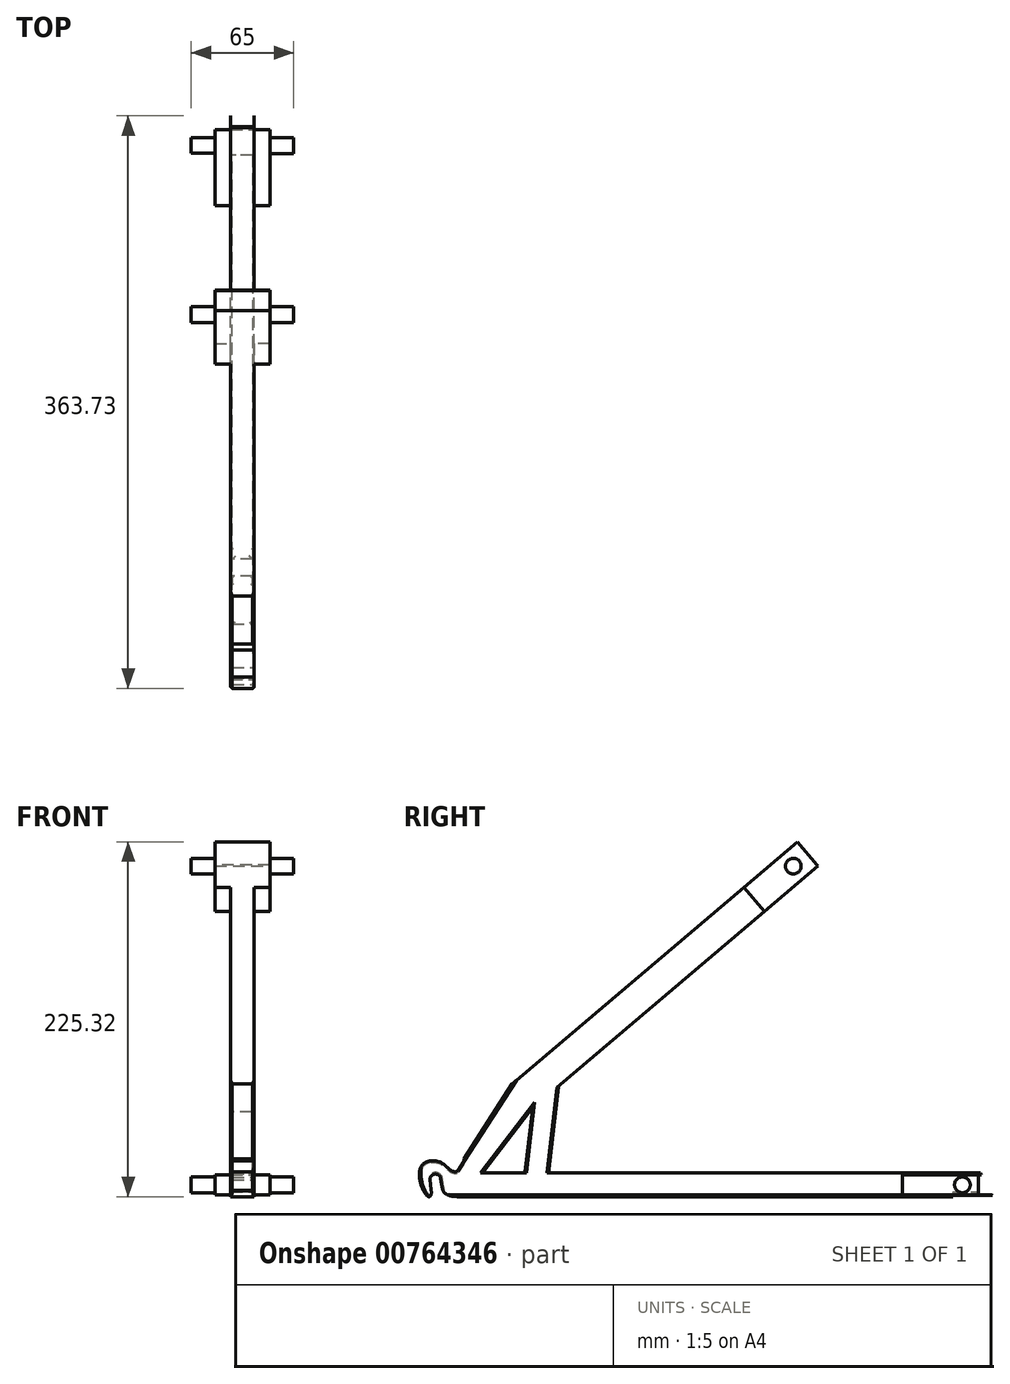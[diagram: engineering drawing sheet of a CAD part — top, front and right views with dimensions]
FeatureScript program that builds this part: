
annotation { "Feature Type Name" : "Feature", "Feature Type Description" : "" }
export const myFeature = defineFeature(function(context is Context, id is Id, definition is map)
    precondition{}
    {
        {
            var Q0;
            Q0=qCreatedBy(makeId("Right.planeOp"),FACE);
            var sketch = newSketch(context, id + "F0", { "sketchPlane" : qUnion([Q0])});
            skLineSegment(sketch, "E0", {"start": v(47.78, 0) * mm, "end": v(315.63, 0) * mm});
            skLineSegment(sketch, "E1", {"start": v(48.64, 41.27) * mm, "end": v(16.93, 0) * mm});
            skLineSegment(sketch, "E2", {"start": v(16.93, 0) * mm, "end": v(47.78, 0) * mm});
            skLineSegment(sketch, "E3.bottom", {"start": v(315.63, 0) * mm, "end": v(16.93, 0) * mm});
            skLineSegment(sketch, "E3.top", {"start": v(315.63, -15) * mm, "end": v(16.93, -15) * mm});
            skLineSegment(sketch, "E3.right", {"start": v(16.93, 0) * mm, "end": v(16.93, -15) * mm});
            skLineSegment(sketch, "E4.left", {"start": v(48.64, 41.27) * mm, "end": v(43.82, 0) * mm});
            skLineSegment(sketch, "E5", {"start": v(48.64, 41.27) * mm, "end": v(35.7, 56.52) * mm});
            skLineSegment(sketch, "E6", {"start": v(16.93, 0) * mm, "end": v(5.04, 9.14) * mm});
            skLineSegment(sketch, "E7", {"start": v(5.04, 9.14) * mm, "end": v(35.7, 56.52) * mm});
            skLineSegment(sketch, "E8", {"start": v(43.82, 0) * mm, "end": v(58.82, 0) * mm});
            skLineSegment(sketch, "E9", {"start": v(58.82, 0) * mm, "end": v(65.3, 55.4) * mm});
            skLineSegment(sketch, "E10", {"start": v(65.3, 55.4) * mm, "end": v(48.64, 41.27) * mm});
            skLineSegment(sketch, "E11", {"start": v(16.93, -15) * mm, "end": v(5.04, -15) * mm});
            skLineSegment(sketch, "E12", {"start": v(5.04, -15) * mm, "end": v(5.04, 9.14) * mm});
            skLineSegment(sketch, "E13", {"start": v(315.63, -15) * mm, "end": v(315.63, 0) * mm});
            skPoint(sketch, "E14", {"position": v(131.02, 137.39) * mm});
            skPoint(sketch, "E15", {"position": v(143.96, 122.14) * mm});
            skPoint(sketch, "E16", {"position": v(115.77, 124.45) * mm});
            skPoint(sketch, "E17", {"position": v(128.7, 109.2) * mm});
            skPoint(sketch, "E18", {"position": v(159.2, 135.07) * mm});
            skPoint(sketch, "E19", {"position": v(146.27, 150.33) * mm});
            skLineSegment(sketch, "E20", {"start": v(128.7, 109.2) * mm, "end": v(115.77, 124.45) * mm});
            skLineSegment(sketch, "E21", {"start": v(35.7, 56.52) * mm, "end": v(48.64, 41.27) * mm});
            skLineSegment(sketch, "E22", {"start": v(146.27, 150.33) * mm, "end": v(159.2, 135.07) * mm});
            skLineSegment(sketch, "E23", {"start": v(35.7, 56.52) * mm, "end": v(115.77, 124.45) * mm});
            skLineSegment(sketch, "E24", {"start": v(65.3, 55.4) * mm, "end": v(128.7, 109.2) * mm});
            skLineSegment(sketch, "E25", {"start": v(115.77, 124.45) * mm, "end": v(146.27, 150.33) * mm});
            skLineSegment(sketch, "E26", {"start": v(128.7, 109.2) * mm, "end": v(159.2, 135.07) * mm});
            skLineSegment(sketch, "E27", {"start": v(229.92, 195.06) * mm, "end": v(216.98, 210.32) * mm});
            skLineSegment(sketch, "E28", {"start": v(159.2, 135.07) * mm, "end": v(229.92, 195.06) * mm});
            skLineSegment(sketch, "E29", {"start": v(216.98, 210.32) * mm, "end": v(146.27, 150.33) * mm});
            skLineSegment(sketch, "E30", {"start": v(340.63, 0) * mm, "end": v(340.63, -15) * mm});
            skLineSegment(sketch, "E31", {"start": v(315.63, 0) * mm, "end": v(340.63, 0) * mm});
            skLineSegment(sketch, "E32", {"start": v(340.63, -15) * mm, "end": v(315.63, -15) * mm});
            skSolve(sketch);
        }
        {
            var Q0;
            {var subQ1=sQuery(id+"F0.wireOp",EDGE,"Yo74uOjQ-i0EO-3RHr-a7oa-XagKDitOUhVE");Q0=makeQuery(id+"F0.imprint","IMPRINT",FACE,{"disambiguationData":[TD([[makeQuery(id+"F0.imprint","IMPRINT",EDGE,{"derivedFrom":subQ1}),1.0]])]});}
            var Q1;
            {var subQ1=sQuery(id+"F0.wireOp",EDGE,"E6");Q1=makeQuery(id+"F0.imprint","IMPRINT",FACE,{"disambiguationData":[TD([[makeQuery(id+"F0.imprint","IMPRINT",EDGE,{"derivedFrom":subQ1}),-1.0]])]});}
            var Q2;
            Q2=makeQuery(id+"F0.imprint","IMPRINT",FACE,{"disambiguationData":[TD([[makeQuery(id+"F0.imprint","IMPRINT",EDGE,{"derivedFrom":sQuery(id+"F0.wireOp",EDGE,"E3.right")}),-1.0]])]});
            var Q3;
            Q3=makeQuery(id+"F0.imprint","IMPRINT",FACE,{"disambiguationData":[TD([[makeQuery(id+"F0.imprint","IMPRINT",EDGE,{"derivedFrom":sQuery(id+"F0.wireOp",EDGE,"E3.top")}),-1.0]])]});
            var Q4;
            {var subQ0=sQuery(id+"F0.wireOp",EDGE,"E4.left");Q4=makeQuery(id+"F0.imprint","IMPRINT",FACE,{"disambiguationData":[TD([[makeQuery(id+"F0.imprint","IMPRINT",EDGE,{"derivedFrom":subQ0}),1.0]])]});}
            var Q5;
            {var subQ3=sQuery(id+"F0.wireOp",EDGE,"RTDkQwoI-wCG5-Ql9m-PHR5-vW7OaOIPGGAD.top");Q5=makeQuery(id+"F0.imprint","IMPRINT",FACE,{"disambiguationData":[TD([[makeQuery(id+"F0.imprint","IMPRINT",EDGE,{"derivedFrom":subQ3}),-1.0]])]});}
            var Q6;
            {var subQ1=sQuery(id+"F0.wireOp",EDGE,"E1");var subQ3=sQuery(id+"F0.wireOp",EDGE,"RTDkQwoI-wCG5-Ql9m-PHR5-vW7OaOIPGGAD.left");var subQ4=makeQuery(id+"F0.imprint","INTERSECT",VERTEX,{"derivedFrom":[subQ1,subQ3]});Q6=makeQuery(id+"F0.imprint","IMPRINT",FACE,{"disambiguationData":[TD([[makeQuery(id+"F0.imprint","IMPRINT",EDGE,{"disambiguationData":[TD([[subQ4,-1.0]])],"derivedFrom":subQ3}),-1.0]])]});}
            var Q7;
            {var subQ0=sQuery(id+"F0.wireOp",EDGE,"o3pL6dEJ-hwyi-6mrB-k6X7-aminsl83ahjA");Q7=makeQuery(id+"F0.imprint","IMPRINT",FACE,{"disambiguationData":[TD([[makeQuery(id+"F0.imprint","IMPRINT",EDGE,{"derivedFrom":subQ0}),-1.0]])]});}
            var Q8;
            {var subQ0=sQuery(id+"F0.wireOp",EDGE,"o3pL6dEJ-hwyi-6mrB-k6X7-aminsl83ahjA");Q8=makeQuery(id+"F0.imprint","IMPRINT",FACE,{"disambiguationData":[TD([[makeQuery(id+"F0.imprint","IMPRINT",EDGE,{"derivedFrom":subQ0}),1.0]])]});}
            var Q9;
            Q9=makeQuery(id+"F0.imprint","IMPRINT",FACE,{"disambiguationData":[TD([[makeQuery(id+"F0.imprint","IMPRINT",EDGE,{"derivedFrom":sQuery(id+"F0.wireOp",EDGE,"Yo74uOjQ-i0EO-3RHr-a7oa-XagKDitOUhVE")}),-1.0]])]});
            var Q10;
            Q10=makeQuery(id+"F0.imprint","IMPRINT",FACE,{"disambiguationData":[TD([[makeQuery(id+"F0.imprint","IMPRINT",EDGE,{"derivedFrom":sQuery(id+"F0.wireOp",EDGE,"WOJb4iod-LhNt-r6cw-RdzF-wMDI1TDEllQv.bottom")}),-1.0]])]});
            var Q11;
            Q11=makeQuery(id+"F0.imprint","IMPRINT",FACE,{"disambiguationData":[TD([[makeQuery(id+"F0.imprint","IMPRINT",EDGE,{"derivedFrom":sQuery(id+"F0.wireOp",EDGE,"WOJb4iod-LhNt-r6cw-RdzF-wMDI1TDEllQv.right")}),1.0]])]});
            var Q12;
            {var subQ0=sQuery(id+"F0.wireOp",EDGE,"E3.right");Q12=makeQuery(id+"F0.imprint","IMPRINT",FACE,{"disambiguationData":[TD([[makeQuery(id+"F0.imprint","IMPRINT",EDGE,{"derivedFrom":subQ0}),1.0]])]});}
            var Q13;
            {var subQ3=sQuery(id+"F0.wireOp",EDGE,"hnlP5vd8-Fwl7-W3YU-HfNq-rofw2tE7fOju");Q13=makeQuery(id+"F0.imprint","IMPRINT",FACE,{"disambiguationData":[TD([[makeQuery(id+"F0.imprint","IMPRINT",EDGE,{"derivedFrom":subQ3}),-1.0]])]});}
            var Q14;
            {var subQ4=sQuery(id+"F0.wireOp",EDGE,"zAPuBMNa-KC0v-FcAM-JJp2-Pc91iyWnGTPB");Q14=makeQuery(id+"F0.imprint","IMPRINT",FACE,{"disambiguationData":[TD([[makeQuery(id+"F0.imprint","IMPRINT",EDGE,{"derivedFrom":subQ4}),-1.0]])]});}
            var Q15;
            {var subQ0=sQuery(id+"F0.wireOp",EDGE,"E3.left");Q15=makeQuery(id+"F0.imprint","IMPRINT",FACE,{"disambiguationData":[TD([[makeQuery(id+"F0.imprint","IMPRINT",EDGE,{"derivedFrom":subQ0}),1.0]])]});}
            var Q16;
            Q16=makeQuery(id+"F0.imprint","IMPRINT",FACE,{"disambiguationData":[TD([[makeQuery(id+"F0.imprint","IMPRINT",EDGE,{"derivedFrom":sQuery(id+"F0.wireOp",EDGE,"E13")}),-1.0]])]});
            var Q17;
            {var subQ2=sQuery(id+"F0.wireOp",EDGE,"Ca3xsWQE-v9L8-s7Dv-516f-RN1bA1puj8tS");Q17=makeQuery(id+"F0.imprint","IMPRINT",FACE,{"disambiguationData":[TD([[makeQuery(id+"F0.imprint","IMPRINT",EDGE,{"derivedFrom":subQ2}),1.0]])]});}
            var Q18;
            {var subQ0=sQuery(id+"F0.wireOp",EDGE,"dxAtwFGu-dCJm-7jaL-4A4g-HOkAJ22Vz9y7");var subQ1=sQuery(id+"F0.wireOp",EDGE,"8YUn9cvo-RZEs-pOM1-VRL8-89LIzTiUGwx0");var subQ2=makeQuery(id+"F0.imprint","INTERSECT",VERTEX,{"derivedFrom":[subQ1,subQ0]});Q18=makeQuery(id+"F0.imprint","IMPRINT",FACE,{"disambiguationData":[TD([[makeQuery(id+"F0.imprint","IMPRINT",EDGE,{"disambiguationData":[TD([[subQ2,-1.0]])],"derivedFrom":subQ0}),1.0]])]});}
            var Q19;
            {var subQ5=sQuery(id+"F0.wireOp",EDGE,"L5jN4jJu-Q4wT-aSny-XyIM-LaIA1ToUzlHX");Q19=makeQuery(id+"F0.imprint","IMPRINT",FACE,{"disambiguationData":[TD([[makeQuery(id+"F0.imprint","IMPRINT",EDGE,{"derivedFrom":subQ5}),1.0]])]});}
            var Q20;
            Q20=makeQuery(id+"F0.imprint","IMPRINT",FACE,{"disambiguationData":[TD([[makeQuery(id+"F0.imprint","IMPRINT",EDGE,{"derivedFrom":sQuery(id+"F0.wireOp",EDGE,"E10")}),-1.0]])]});
            var Q21;
            Q21=makeQuery(id+"F0.imprint","IMPRINT",FACE,{"disambiguationData":[TD([[makeQuery(id+"F0.imprint","IMPRINT",EDGE,{"derivedFrom":sQuery(id+"F0.wireOp",EDGE,"E22")}),1.0]])]});
            var Q22;
            Q22=makeQuery(id+"F0.imprint","IMPRINT",FACE,{"disambiguationData":[TD([[makeQuery(id+"F0.imprint","IMPRINT",EDGE,{"derivedFrom":sQuery(id+"F0.wireOp",EDGE,"E20")}),-1.0]])]});
            extrude(context, id + "F1", {"entities" : qUnion([Q0, Q1, Q2, Q3, Q4, Q5, Q6, Q7, Q8, Q9, Q10, Q11, Q12, Q13, Q14, Q15, Q16, Q17, Q18, Q19, Q20, Q21, Q22]), "depth" : 15 * mm, "offsetDistance" : 25 * mm});
        }
        {
            var Q0;
            {var subQ0=sQuery(id+"F0.wireOp",EDGE,"E3.bottom");Q0=makeQuery(id+"F1.opExtrude","CAP_EDGE",EDGE,{"disambiguationData":[OSD([subQ0]),TDD([makeQuery(id+"F0.imprint","IMPRINT",EDGE,{"disambiguationData":[TD([[makeQuery(id+"F0.imprint","INTERSECT",VERTEX,{"derivedFrom":[subQ0,sQuery(id+"F0.wireOp",EDGE,"E3.left")]}),-1.0]])],"derivedFrom":subQ0})])],"isStart":false});}
            var Q1;
            {var subQ0=sQuery(id+"F0.wireOp",EDGE,"E3.bottom");Q1=makeQuery(id+"F1.opExtrude","CAP_EDGE",EDGE,{"disambiguationData":[OSD([subQ0]),TDD([makeQuery(id+"F0.imprint","IMPRINT",EDGE,{"disambiguationData":[TD([[makeQuery(id+"F0.imprint","INTERSECT",VERTEX,{"derivedFrom":[subQ0,sQuery(id+"F0.wireOp",EDGE,"E3.left")]}),-1.0]])],"derivedFrom":subQ0})])],"isStart":true});}
            var Q2;
            Q2=makeQuery(id+"F1.opExtrude","CAP_EDGE",EDGE,{"disambiguationData":[OSD([sQuery(id+"F0.wireOp",EDGE,"E3.top")])],"isStart":true});
            var Q3;
            Q3=makeQuery(id+"F1.opExtrude","CAP_EDGE",EDGE,{"disambiguationData":[OSD([sQuery(id+"F0.wireOp",EDGE,"E3.top")])],"isStart":false});
            var Q4;
            Q4=makeQuery(id+"F1.opExtrude","CAP_EDGE",EDGE,{"disambiguationData":[OSD([sQuery(id+"F0.wireOp",EDGE,"E3.left")])],"isStart":false});
            var Q5;
            Q5=makeQuery(id+"F1.opExtrude","SWEPT_EDGE",EDGE,{"disambiguationData":[OSD([sQuery(id+"F0.wireOp",EDGE,"E3.bottom"),sQuery(id+"F0.wireOp",EDGE,"E3.left")])]});
            var Q6;
            Q6=makeQuery(id+"F1.opExtrude","CAP_EDGE",EDGE,{"disambiguationData":[OSD([sQuery(id+"F0.wireOp",EDGE,"E3.left")])],"isStart":true});
            var Q7;
            Q7=makeQuery(id+"F1.opExtrude","SWEPT_EDGE",EDGE,{"disambiguationData":[OSD([sQuery(id+"F0.wireOp",EDGE,"E3.top"),sQuery(id+"F0.wireOp",EDGE,"E3.left")])]});
            var Q8;
            Q8=makeQuery(id+"F1.opExtrude","CAP_EDGE",EDGE,{"disambiguationData":[OSD([sQuery(id+"F0.wireOp",EDGE,"d41c5ef0-c10e-4e75-b374-802d414c0d57")])],"isStart":false});
            var Q9;
            Q9=makeQuery(id+"F1.opExtrude","CAP_EDGE",EDGE,{"disambiguationData":[OSD([sQuery(id+"F0.wireOp",EDGE,"d41c5ef0-c10e-4e75-b374-802d414c0d57")])],"isStart":true});
            var Q10;
            Q10=makeQuery(id+"F1.opExtrude","CAP_EDGE",EDGE,{"disambiguationData":[OSD([sQuery(id+"F0.wireOp",EDGE,"E1")])],"isStart":false});
            var Q11;
            Q11=makeQuery(id+"F1.opExtrude","CAP_EDGE",EDGE,{"disambiguationData":[OSD([sQuery(id+"F0.wireOp",EDGE,"E4.left")])],"isStart":false});
            var Q12;
            {var subQ0=sQuery(id+"F0.wireOp",EDGE,"E3.bottom");Q12=makeQuery(id+"F1.opExtrude","CAP_EDGE",EDGE,{"disambiguationData":[OSD([subQ0]),TDD([makeQuery(id+"F0.imprint","IMPRINT",EDGE,{"disambiguationData":[TD([[makeQuery(id+"F0.imprint","INTERSECT",VERTEX,{"derivedFrom":[subQ0,sQuery(id+"F0.wireOp",EDGE,"E4.left"),sQuery(id+"F0.wireOp",EDGE,"E8")]}),-1.0]])],"derivedFrom":subQ0})])],"isStart":false});}
            var Q13;
            Q13=makeQuery(id+"F1.opExtrude","CAP_EDGE",EDGE,{"disambiguationData":[OSD([sQuery(id+"F0.wireOp",EDGE,"E9")])],"isStart":false});
            var Q14;
            Q14=makeQuery(id+"F1.opExtrude","CAP_EDGE",EDGE,{"disambiguationData":[OSD([sQuery(id+"F0.wireOp",EDGE,"E7")])],"isStart":false});
            var Q15;
            Q15=makeQuery(id+"F1.opExtrude","CAP_EDGE",EDGE,{"disambiguationData":[OSD([sQuery(id+"F0.wireOp",EDGE,"E7")])],"isStart":true});
            var Q16;
            Q16=makeQuery(id+"F1.opExtrude","CAP_EDGE",EDGE,{"disambiguationData":[OSD([sQuery(id+"F0.wireOp",EDGE,"E1")])],"isStart":true});
            var Q17;
            Q17=makeQuery(id+"F1.opExtrude","CAP_EDGE",EDGE,{"disambiguationData":[OSD([sQuery(id+"F0.wireOp",EDGE,"E4.left")])],"isStart":true});
            var Q18;
            {var subQ0=sQuery(id+"F0.wireOp",EDGE,"E3.bottom");Q18=makeQuery(id+"F1.opExtrude","CAP_EDGE",EDGE,{"disambiguationData":[OSD([subQ0]),TDD([makeQuery(id+"F0.imprint","IMPRINT",EDGE,{"disambiguationData":[TD([[makeQuery(id+"F0.imprint","INTERSECT",VERTEX,{"derivedFrom":[subQ0,sQuery(id+"F0.wireOp",EDGE,"E4.left"),sQuery(id+"F0.wireOp",EDGE,"E8")]}),-1.0]])],"derivedFrom":subQ0})])],"isStart":true});}
            var Q19;
            Q19=makeQuery(id+"F1.opExtrude","CAP_EDGE",EDGE,{"disambiguationData":[OSD([sQuery(id+"F0.wireOp",EDGE,"E9")])],"isStart":true});
            var Q20;
            Q20=makeQuery(id+"F1.opExtrude","CAP_EDGE",EDGE,{"disambiguationData":[OSD([sQuery(id+"F0.wireOp",EDGE,"uIqcDY9T-Jbxf-aRt4-gg0R-6jHuYA81VSVm")])],"isStart":true});
            var Q21;
            Q21=makeQuery(id+"F1.opExtrude","CAP_EDGE",EDGE,{"disambiguationData":[OSD([sQuery(id+"F0.wireOp",EDGE,"uIqcDY9T-Jbxf-aRt4-gg0R-6jHuYA81VSVm")])],"isStart":false});
            var Q22;
            Q22=makeQuery(id+"F1.opExtrude","CAP_EDGE",EDGE,{"disambiguationData":[OSD([sQuery(id+"F0.wireOp",EDGE,"rEmcZTTS-8Wlh-duEK-OSmW-KXRGUTnN0HfS")])],"isStart":true});
            var Q23;
            Q23=makeQuery(id+"F1.opExtrude","CAP_EDGE",EDGE,{"disambiguationData":[OSD([sQuery(id+"F0.wireOp",EDGE,"rEmcZTTS-8Wlh-duEK-OSmW-KXRGUTnN0HfS")])],"isStart":false});
            var Q24;
            Q24=makeQuery(id+"F1.opExtrude","CAP_EDGE",EDGE,{"disambiguationData":[OSD([sQuery(id+"F0.wireOp",EDGE,"d98010bc-28d3-49a1-b6f3-b908af7b2b54")])],"isStart":false});
            var Q25;
            Q25=makeQuery(id+"F1.opExtrude","CAP_EDGE",EDGE,{"disambiguationData":[OSD([sQuery(id+"F0.wireOp",EDGE,"d98010bc-28d3-49a1-b6f3-b908af7b2b54")])],"isStart":true});
            var Q26;
            Q26=makeQuery(id+"F1.opExtrude","CAP_EDGE",EDGE,{"disambiguationData":[OSD([sQuery(id+"F0.wireOp",EDGE,"WOJb4iod-LhNt-r6cw-RdzF-wMDI1TDEllQv.bottom")])],"isStart":false});
            var Q27;
            Q27=makeQuery(id+"F1.opExtrude","CAP_EDGE",EDGE,{"disambiguationData":[OSD([sQuery(id+"F0.wireOp",EDGE,"WOJb4iod-LhNt-r6cw-RdzF-wMDI1TDEllQv.bottom")])],"isStart":true});
            var Q28;
            Q28=makeQuery(id+"F1.opExtrude","CAP_EDGE",EDGE,{"disambiguationData":[OSD([sQuery(id+"F0.wireOp",EDGE,"ba8b6f3e-864d-4f68-a7dd-abca2b296de0")])],"isStart":false});
            var Q29;
            Q29=makeQuery(id+"F1.opExtrude","CAP_EDGE",EDGE,{"disambiguationData":[OSD([sQuery(id+"F0.wireOp",EDGE,"ba8b6f3e-864d-4f68-a7dd-abca2b296de0")])],"isStart":true});
            var Q30;
            Q30=makeQuery(id+"F1.opExtrude","CAP_EDGE",EDGE,{"disambiguationData":[OSD([sQuery(id+"F0.wireOp",EDGE,"600a4db5-ffff-4d01-831d-9f2957b33658")])],"isStart":false});
            var Q31;
            Q31=makeQuery(id+"F1.opExtrude","CAP_EDGE",EDGE,{"disambiguationData":[OSD([sQuery(id+"F0.wireOp",EDGE,"WOJb4iod-LhNt-r6cw-RdzF-wMDI1TDEllQv.top")])],"isStart":false});
            var Q32;
            Q32=makeQuery(id+"F1.opExtrude","CAP_EDGE",EDGE,{"disambiguationData":[OSD([sQuery(id+"F0.wireOp",EDGE,"efedae53-bb98-4f59-96c4-10e90d9c938b")])],"isStart":false});
            var Q33;
            Q33=makeQuery(id+"F1.opExtrude","CAP_EDGE",EDGE,{"disambiguationData":[OSD([sQuery(id+"F0.wireOp",EDGE,"CVsaIfdG-YInH-x2fQ-98NN-BXrdCocnHfCg")])],"isStart":false});
            var Q34;
            Q34=makeQuery(id+"F1.opExtrude","CAP_EDGE",EDGE,{"disambiguationData":[OSD([sQuery(id+"F0.wireOp",EDGE,"NhF1xUkv-KuKP-hu54-HcND-xiFQGb7Tj3II")])],"isStart":false});
            var Q35;
            Q35=makeQuery(id+"F1.opExtrude","CAP_EDGE",EDGE,{"disambiguationData":[OSD([sQuery(id+"F0.wireOp",EDGE,"CVsaIfdG-YInH-x2fQ-98NN-BXrdCocnHfCg")])],"isStart":true});
            var Q36;
            Q36=makeQuery(id+"F1.opExtrude","CAP_EDGE",EDGE,{"disambiguationData":[OSD([sQuery(id+"F0.wireOp",EDGE,"NhF1xUkv-KuKP-hu54-HcND-xiFQGb7Tj3II")])],"isStart":true});
            var Q37;
            Q37=makeQuery(id+"F1.opExtrude","CAP_EDGE",EDGE,{"disambiguationData":[OSD([sQuery(id+"F0.wireOp",EDGE,"efedae53-bb98-4f59-96c4-10e90d9c938b")])],"isStart":true});
            var Q38;
            Q38=makeQuery(id+"F1.opExtrude","CAP_EDGE",EDGE,{"disambiguationData":[OSD([sQuery(id+"F0.wireOp",EDGE,"WOJb4iod-LhNt-r6cw-RdzF-wMDI1TDEllQv.top")])],"isStart":true});
            var Q39;
            Q39=makeQuery(id+"F1.opExtrude","CAP_EDGE",EDGE,{"disambiguationData":[OSD([sQuery(id+"F0.wireOp",EDGE,"600a4db5-ffff-4d01-831d-9f2957b33658")])],"isStart":true});
            chamfer(context, id + "F2", {"entities" : qUnion([Q0, Q1, Q2, Q3, Q4, Q5, Q6, Q7, Q8, Q9, Q10, Q11, Q12, Q13, Q14, Q15, Q16, Q17, Q18, Q19, Q20, Q21, Q22, Q23, Q24, Q25, Q26, Q27, Q28, Q29, Q30, Q31, Q32, Q33, Q34, Q35, Q36, Q37, Q38, Q39]), "width" : 1 * mm, "tangentPropagation" : true});
        }
        {
            var Q0;
            Q0=makeQuery(id+"F1.opExtrude","SWEPT_EDGE",EDGE,{"disambiguationData":[OSD([sQuery(id+"F0.wireOp",EDGE,"E3.bottom"),sQuery(id+"F0.wireOp",EDGE,"E8"),sQuery(id+"F0.wireOp",EDGE,"E9")])]});
            var Q1;
            Q1=makeQuery(id+"F1.opExtrude","SWEPT_EDGE",EDGE,{"disambiguationData":[OSD([sQuery(id+"F0.wireOp",EDGE,"uIqcDY9T-Jbxf-aRt4-gg0R-6jHuYA81VSVm"),sQuery(id+"F0.wireOp",EDGE,"E9"),sQuery(id+"F0.wireOp",EDGE,"E10")])]});
            fillet(context, id + "F3", {"entities" : qUnion([Q0, Q1]), "radius" : 2 * mm, "tangentPropagation" : true, "allowEdgeOverflow" : false});
        }
        {
            var Q0;
            Q0=makeQuery(id+"F1.opExtrude","SWEPT_EDGE",EDGE,{"disambiguationData":[OSD([sQuery(id+"F0.wireOp",EDGE,"E3.bottom"),sQuery(id+"F0.wireOp",EDGE,"E4.left"),sQuery(id+"F0.wireOp",EDGE,"E8")])]});
            var Q1;
            Q1=makeQuery(id+"F1.opExtrude","SWEPT_EDGE",EDGE,{"disambiguationData":[OSD([sQuery(id+"F0.wireOp",EDGE,"E1"),sQuery(id+"F0.wireOp",EDGE,"E3.bottom"),sQuery(id+"F0.wireOp",EDGE,"E3.right"),sQuery(id+"F0.wireOp",EDGE,"E6")])]});
            var Q2;
            Q2=makeQuery(id+"F1.opExtrude","SWEPT_EDGE",EDGE,{"disambiguationData":[OSD([sQuery(id+"F0.wireOp",EDGE,"E1"),sQuery(id+"F0.wireOp",EDGE,"E4.left"),sQuery(id+"F0.wireOp",EDGE,"E5"),sQuery(id+"F0.wireOp",EDGE,"E10")])]});
            fillet(context, id + "F4", {"entities" : qUnion([Q0, Q1, Q2]), "radius" : 1 * mm, "tangentPropagation" : true, "allowEdgeOverflow" : false});
        }
        {
            var Q0;
            Q0=makeQuery(id+"F1.opExtrude","SWEPT_FACE",FACE,{"disambiguationData":[OSD([sQuery(id+"F0.wireOp",EDGE,"E12")])]});
            var sketch = newSketch(context, id + "F5", { "sketchPlane" : qUnion([Q0])});
            skLineSegment(sketch, "E33.bottom", {"start": v(0, -15) * mm, "end": v(15, -15) * mm});
            skLineSegment(sketch, "E33.top", {"start": v(0, 9.14) * mm, "end": v(15, 9.14) * mm});
            skLineSegment(sketch, "E33.left", {"start": v(0, -15) * mm, "end": v(0, 9.14) * mm});
            skLineSegment(sketch, "E33.right", {"start": v(15, -15) * mm, "end": v(15, 9.14) * mm});
            skSolve(sketch);
        }
        {
            var Q0;
            Q0=qSketchRegion(id+"F5",true);
            extrude(context, id + "F6", {"entities" : qUnion([Q0]), "operationType" : NewBodyOperationType.ADD, "depth" : 35 * mm, "offsetDistance" : 25 * mm});
        }
        {
            var Q0;
            Q0=makeQuery(id+"F6.boolean.opBoolean","MERGE",FACE,{"derivedFrom":[makeQuery(id+"F2.opChamfer","SPLIT",FACE,{"disambiguationData":[OD(0.0)],"derivedFrom":makeQuery(id+"F1.opExtrude","CAP_FACE",FACE,{"disambiguationData":[OSD([sQuery(id+"F0.wireOp",EDGE,"uIqcDY9T-Jbxf-aRt4-gg0R-6jHuYA81VSVm"),sQuery(id+"F0.wireOp",EDGE,"E1"),sQuery(id+"F0.wireOp",EDGE,"E3.bottom"),sQuery(id+"F0.wireOp",EDGE,"E3.top"),sQuery(id+"F0.wireOp",EDGE,"E3.left"),sQuery(id+"F0.wireOp",EDGE,"E4.left"),sQuery(id+"F0.wireOp",EDGE,"rEmcZTTS-8Wlh-duEK-OSmW-KXRGUTnN0HfS"),sQuery(id+"F0.wireOp",EDGE,"E7"),sQuery(id+"F0.wireOp",EDGE,"E9"),sQuery(id+"F0.wireOp",EDGE,"d98010bc-28d3-49a1-b6f3-b908af7b2b54"),sQuery(id+"F0.wireOp",EDGE,"600a4db5-ffff-4d01-831d-9f2957b33658"),sQuery(id+"F0.wireOp",EDGE,"WOJb4iod-LhNt-r6cw-RdzF-wMDI1TDEllQv.bottom"),sQuery(id+"F0.wireOp",EDGE,"WOJb4iod-LhNt-r6cw-RdzF-wMDI1TDEllQv.top"),sQuery(id+"F0.wireOp",EDGE,"NhF1xUkv-KuKP-hu54-HcND-xiFQGb7Tj3II"),sQuery(id+"F0.wireOp",EDGE,"efedae53-bb98-4f59-96c4-10e90d9c938b"),sQuery(id+"F0.wireOp",EDGE,"ba8b6f3e-864d-4f68-a7dd-abca2b296de0"),sQuery(id+"F0.wireOp",EDGE,"CVsaIfdG-YInH-x2fQ-98NN-BXrdCocnHfCg"),sQuery(id+"F0.wireOp",EDGE,"00UZXHGD-P9IW-BGjO-shcO-QPdciv9J71iY"),sQuery(id+"F0.wireOp",EDGE,"a7nKF1FW-fnAZ-2znJ-PXXG-xkcUWXIHMq71"),sQuery(id+"F0.wireOp",EDGE,"E11"),sQuery(id+"F0.wireOp",EDGE,"E12")])],"isStart":false})}),makeQuery(id+"F6.opExtrude","SWEPT_FACE",FACE,{"disambiguationData":[OSD([sQuery(id+"F5.wireOp",EDGE,"E33.right")])]})]});
            var sketch = newSketch(context, id + "F7", { "sketchPlane" : qUnion([Q0])});
            skLineSegment(sketch, "E34", {"start": v(5.04, 7.3) * mm, "end": v(1.23, 1.42) * mm});
            skPoint(sketch, "E35", {"position": v(-15.29, -15) * mm});
            skPoint(sketch, "E36", {"position": v(-8.29, -15) * mm});
            skFitSpline(sketch, "E37", {"points": [v(-15.81, -10.33) * mm, v(-16.74, -15) * mm, v(-20.68, -11.17) * mm], "startDerivative": vector(3.5, -16.33) * mm, "endDerivative": vector(-10.01, 17.22) * mm});
            skArc(sketch, "E38", {"start": v(-9.8, -2.74) * mm, "mid": v(-13.78, -0.75) * mm, "end": v(-16.49, -4.3) * mm});
            skFitSpline(sketch, "E39", {"points": [v(-23.08, 0.68) * mm, v(-23.08, -3.12) * mm, v(-20.68, -11.17) * mm], "startDerivative": vector(0.94, -17.18) * mm, "endDerivative": vector(7.79, -14.34) * mm});
            skLineSegment(sketch, "E40", {"start": v(-16.49, -4.3) * mm, "end": v(-15.81, -10.33) * mm});
            skFitSpline(sketch, "E41", {"points": [v(-9.8, -2.74) * mm, v(-6.92, -12.83) * mm, v(5.04, -15) * mm], "startDerivative": vector(3.63, -23.4) * mm, "endDerivative": vector(29.15, 0) * mm});
            skArc(sketch, "E42", {"start": v(-15.82, 7.7) * mm, "mid": v(-20.83, 5.61) * mm, "end": v(-23.08, 0.68) * mm});
            skFitSpline(sketch, "E43", {"points": [v(1.23, 1.42) * mm, v(-6.2, 4.2) * mm, v(-15.82, 7.7) * mm], "startDerivative": vector(-16.53, -11.89) * mm, "endDerivative": vector(-29.61, -1.65) * mm});
            skLineSegment(sketch, "E44", {"start": v(5.04, 7.3) * mm, "end": v(5.04, -15) * mm});
            skSolve(sketch);
        }
        {
            var Q0;
            Q0=makeQuery(id+"F7.imprint","IMPRINT",FACE,{"disambiguationData":[TD([[makeQuery(id+"F7.imprint","IMPRINT",EDGE,{"derivedFrom":sQuery(id+"F7.wireOp",EDGE,"E34")}),-1.0]])]});
            var Q1;
            {var subQ1=sQuery(id+"F7.wireOp",EDGE,"E38");Q1=makeQuery(id+"F7.imprint","IMPRINT",FACE,{"disambiguationData":[TD([[makeQuery(id+"F7.imprint","IMPRINT",EDGE,{"derivedFrom":subQ1}),1.0]])]});}
            extrude(context, id + "F8", {"entities" : qUnion([Q0, Q1]), "operationType" : NewBodyOperationType.REMOVE, "oppositeDirection" : true, "depth" : 25 * mm, "offsetDistance" : 25 * mm});
        }
        {
            var Q0;
            Q0=makeQuery(id+"F8.boolean.opBoolean","COPY",EDGE,{"derivedFrom":makeQuery(id+"F8.opExtrude","CAP_EDGE",EDGE,{"disambiguationData":[OSD([sQuery(id+"F7.wireOp",EDGE,"E43")])],"isStart":true})});
            var Q1;
            Q1=makeQuery(id+"F8.boolean.opBoolean","INTERSECT",EDGE,{"derivedFrom":[makeQuery(id+"F6.boolean.opBoolean","MERGE",FACE,{"derivedFrom":[makeQuery(id+"F2.opChamfer","SPLIT",FACE,{"disambiguationData":[OD(0.0)],"derivedFrom":makeQuery(id+"F1.opExtrude","CAP_FACE",FACE,{"disambiguationData":[OSD([sQuery(id+"F0.wireOp",EDGE,"uIqcDY9T-Jbxf-aRt4-gg0R-6jHuYA81VSVm"),sQuery(id+"F0.wireOp",EDGE,"E1"),sQuery(id+"F0.wireOp",EDGE,"E3.bottom"),sQuery(id+"F0.wireOp",EDGE,"E3.top"),sQuery(id+"F0.wireOp",EDGE,"E3.left"),sQuery(id+"F0.wireOp",EDGE,"E4.left"),sQuery(id+"F0.wireOp",EDGE,"rEmcZTTS-8Wlh-duEK-OSmW-KXRGUTnN0HfS"),sQuery(id+"F0.wireOp",EDGE,"E7"),sQuery(id+"F0.wireOp",EDGE,"E9"),sQuery(id+"F0.wireOp",EDGE,"d98010bc-28d3-49a1-b6f3-b908af7b2b54"),sQuery(id+"F0.wireOp",EDGE,"600a4db5-ffff-4d01-831d-9f2957b33658"),sQuery(id+"F0.wireOp",EDGE,"WOJb4iod-LhNt-r6cw-RdzF-wMDI1TDEllQv.bottom"),sQuery(id+"F0.wireOp",EDGE,"WOJb4iod-LhNt-r6cw-RdzF-wMDI1TDEllQv.top"),sQuery(id+"F0.wireOp",EDGE,"NhF1xUkv-KuKP-hu54-HcND-xiFQGb7Tj3II"),sQuery(id+"F0.wireOp",EDGE,"efedae53-bb98-4f59-96c4-10e90d9c938b"),sQuery(id+"F0.wireOp",EDGE,"ba8b6f3e-864d-4f68-a7dd-abca2b296de0"),sQuery(id+"F0.wireOp",EDGE,"CVsaIfdG-YInH-x2fQ-98NN-BXrdCocnHfCg"),sQuery(id+"F0.wireOp",EDGE,"00UZXHGD-P9IW-BGjO-shcO-QPdciv9J71iY"),sQuery(id+"F0.wireOp",EDGE,"a7nKF1FW-fnAZ-2znJ-PXXG-xkcUWXIHMq71"),sQuery(id+"F0.wireOp",EDGE,"E11"),sQuery(id+"F0.wireOp",EDGE,"E12")])],"isStart":true})}),makeQuery(id+"F6.opExtrude","SWEPT_FACE",FACE,{"disambiguationData":[OSD([sQuery(id+"F5.wireOp",EDGE,"E33.left")])]})]}),makeQuery(id+"F8.opExtrude","SWEPT_FACE",FACE,{"disambiguationData":[OSD([sQuery(id+"F7.wireOp",EDGE,"E43")])]})]});
            var Q2;
            Q2=makeQuery(id+"F8.boolean.opBoolean","COPY",EDGE,{"derivedFrom":makeQuery(id+"F8.opExtrude","CAP_EDGE",EDGE,{"disambiguationData":[OSD([sQuery(id+"F7.wireOp",EDGE,"E42")])],"isStart":true})});
            var Q3;
            Q3=makeQuery(id+"F8.boolean.opBoolean","INTERSECT",EDGE,{"derivedFrom":[makeQuery(id+"F6.boolean.opBoolean","MERGE",FACE,{"derivedFrom":[makeQuery(id+"F2.opChamfer","SPLIT",FACE,{"disambiguationData":[OD(0.0)],"derivedFrom":makeQuery(id+"F1.opExtrude","CAP_FACE",FACE,{"disambiguationData":[OSD([sQuery(id+"F0.wireOp",EDGE,"uIqcDY9T-Jbxf-aRt4-gg0R-6jHuYA81VSVm"),sQuery(id+"F0.wireOp",EDGE,"E1"),sQuery(id+"F0.wireOp",EDGE,"E3.bottom"),sQuery(id+"F0.wireOp",EDGE,"E3.top"),sQuery(id+"F0.wireOp",EDGE,"E3.left"),sQuery(id+"F0.wireOp",EDGE,"E4.left"),sQuery(id+"F0.wireOp",EDGE,"rEmcZTTS-8Wlh-duEK-OSmW-KXRGUTnN0HfS"),sQuery(id+"F0.wireOp",EDGE,"E7"),sQuery(id+"F0.wireOp",EDGE,"E9"),sQuery(id+"F0.wireOp",EDGE,"d98010bc-28d3-49a1-b6f3-b908af7b2b54"),sQuery(id+"F0.wireOp",EDGE,"600a4db5-ffff-4d01-831d-9f2957b33658"),sQuery(id+"F0.wireOp",EDGE,"WOJb4iod-LhNt-r6cw-RdzF-wMDI1TDEllQv.bottom"),sQuery(id+"F0.wireOp",EDGE,"WOJb4iod-LhNt-r6cw-RdzF-wMDI1TDEllQv.top"),sQuery(id+"F0.wireOp",EDGE,"NhF1xUkv-KuKP-hu54-HcND-xiFQGb7Tj3II"),sQuery(id+"F0.wireOp",EDGE,"efedae53-bb98-4f59-96c4-10e90d9c938b"),sQuery(id+"F0.wireOp",EDGE,"ba8b6f3e-864d-4f68-a7dd-abca2b296de0"),sQuery(id+"F0.wireOp",EDGE,"CVsaIfdG-YInH-x2fQ-98NN-BXrdCocnHfCg"),sQuery(id+"F0.wireOp",EDGE,"00UZXHGD-P9IW-BGjO-shcO-QPdciv9J71iY"),sQuery(id+"F0.wireOp",EDGE,"a7nKF1FW-fnAZ-2znJ-PXXG-xkcUWXIHMq71"),sQuery(id+"F0.wireOp",EDGE,"E11"),sQuery(id+"F0.wireOp",EDGE,"E12")])],"isStart":true})}),makeQuery(id+"F6.opExtrude","SWEPT_FACE",FACE,{"disambiguationData":[OSD([sQuery(id+"F5.wireOp",EDGE,"E33.left")])]})]}),makeQuery(id+"F8.opExtrude","SWEPT_FACE",FACE,{"disambiguationData":[OSD([sQuery(id+"F7.wireOp",EDGE,"E42")])]})]});
            var Q4;
            Q4=makeQuery(id+"F8.boolean.opBoolean","COPY",EDGE,{"derivedFrom":makeQuery(id+"F8.opExtrude","CAP_EDGE",EDGE,{"disambiguationData":[OSD([sQuery(id+"F7.wireOp",EDGE,"E34")])],"isStart":true})});
            var Q5;
            Q5=makeQuery(id+"F8.boolean.opBoolean","INTERSECT",EDGE,{"derivedFrom":[makeQuery(id+"F6.boolean.opBoolean","MERGE",FACE,{"derivedFrom":[makeQuery(id+"F2.opChamfer","SPLIT",FACE,{"disambiguationData":[OD(0.0)],"derivedFrom":makeQuery(id+"F1.opExtrude","CAP_FACE",FACE,{"disambiguationData":[OSD([sQuery(id+"F0.wireOp",EDGE,"uIqcDY9T-Jbxf-aRt4-gg0R-6jHuYA81VSVm"),sQuery(id+"F0.wireOp",EDGE,"E1"),sQuery(id+"F0.wireOp",EDGE,"E3.bottom"),sQuery(id+"F0.wireOp",EDGE,"E3.top"),sQuery(id+"F0.wireOp",EDGE,"E3.left"),sQuery(id+"F0.wireOp",EDGE,"E4.left"),sQuery(id+"F0.wireOp",EDGE,"rEmcZTTS-8Wlh-duEK-OSmW-KXRGUTnN0HfS"),sQuery(id+"F0.wireOp",EDGE,"E7"),sQuery(id+"F0.wireOp",EDGE,"E9"),sQuery(id+"F0.wireOp",EDGE,"d98010bc-28d3-49a1-b6f3-b908af7b2b54"),sQuery(id+"F0.wireOp",EDGE,"600a4db5-ffff-4d01-831d-9f2957b33658"),sQuery(id+"F0.wireOp",EDGE,"WOJb4iod-LhNt-r6cw-RdzF-wMDI1TDEllQv.bottom"),sQuery(id+"F0.wireOp",EDGE,"WOJb4iod-LhNt-r6cw-RdzF-wMDI1TDEllQv.top"),sQuery(id+"F0.wireOp",EDGE,"NhF1xUkv-KuKP-hu54-HcND-xiFQGb7Tj3II"),sQuery(id+"F0.wireOp",EDGE,"efedae53-bb98-4f59-96c4-10e90d9c938b"),sQuery(id+"F0.wireOp",EDGE,"ba8b6f3e-864d-4f68-a7dd-abca2b296de0"),sQuery(id+"F0.wireOp",EDGE,"CVsaIfdG-YInH-x2fQ-98NN-BXrdCocnHfCg"),sQuery(id+"F0.wireOp",EDGE,"00UZXHGD-P9IW-BGjO-shcO-QPdciv9J71iY"),sQuery(id+"F0.wireOp",EDGE,"a7nKF1FW-fnAZ-2znJ-PXXG-xkcUWXIHMq71"),sQuery(id+"F0.wireOp",EDGE,"E11"),sQuery(id+"F0.wireOp",EDGE,"E12")])],"isStart":true})}),makeQuery(id+"F6.opExtrude","SWEPT_FACE",FACE,{"disambiguationData":[OSD([sQuery(id+"F5.wireOp",EDGE,"E33.left")])]})]}),makeQuery(id+"F8.opExtrude","SWEPT_FACE",FACE,{"disambiguationData":[OSD([sQuery(id+"F7.wireOp",EDGE,"E34")])]})]});
            var Q6;
            Q6=makeQuery(id+"F8.boolean.opBoolean","COPY",EDGE,{"derivedFrom":makeQuery(id+"F8.opExtrude","CAP_EDGE",EDGE,{"disambiguationData":[OSD([sQuery(id+"F7.wireOp",EDGE,"E39")])],"isStart":true})});
            var Q7;
            Q7=makeQuery(id+"F8.boolean.opBoolean","COPY",FACE,{"derivedFrom":makeQuery(id+"F8.opExtrude","SWEPT_FACE",FACE,{"disambiguationData":[OSD([sQuery(id+"F7.wireOp",EDGE,"E39")])]})});
            var Q8;
            Q8=makeQuery(id+"F8.boolean.opBoolean","COPY",EDGE,{"derivedFrom":makeQuery(id+"F8.opExtrude","CAP_EDGE",EDGE,{"disambiguationData":[OSD([sQuery(id+"F7.wireOp",EDGE,"E38")])],"isStart":true})});
            var Q9;
            Q9=makeQuery(id+"F8.boolean.opBoolean","INTERSECT",EDGE,{"derivedFrom":[makeQuery(id+"F6.boolean.opBoolean","MERGE",FACE,{"derivedFrom":[makeQuery(id+"F2.opChamfer","SPLIT",FACE,{"disambiguationData":[OD(0.0)],"derivedFrom":makeQuery(id+"F1.opExtrude","CAP_FACE",FACE,{"disambiguationData":[OSD([sQuery(id+"F0.wireOp",EDGE,"uIqcDY9T-Jbxf-aRt4-gg0R-6jHuYA81VSVm"),sQuery(id+"F0.wireOp",EDGE,"E1"),sQuery(id+"F0.wireOp",EDGE,"E3.bottom"),sQuery(id+"F0.wireOp",EDGE,"E3.top"),sQuery(id+"F0.wireOp",EDGE,"E3.left"),sQuery(id+"F0.wireOp",EDGE,"E4.left"),sQuery(id+"F0.wireOp",EDGE,"rEmcZTTS-8Wlh-duEK-OSmW-KXRGUTnN0HfS"),sQuery(id+"F0.wireOp",EDGE,"E7"),sQuery(id+"F0.wireOp",EDGE,"E9"),sQuery(id+"F0.wireOp",EDGE,"d98010bc-28d3-49a1-b6f3-b908af7b2b54"),sQuery(id+"F0.wireOp",EDGE,"600a4db5-ffff-4d01-831d-9f2957b33658"),sQuery(id+"F0.wireOp",EDGE,"WOJb4iod-LhNt-r6cw-RdzF-wMDI1TDEllQv.bottom"),sQuery(id+"F0.wireOp",EDGE,"WOJb4iod-LhNt-r6cw-RdzF-wMDI1TDEllQv.top"),sQuery(id+"F0.wireOp",EDGE,"NhF1xUkv-KuKP-hu54-HcND-xiFQGb7Tj3II"),sQuery(id+"F0.wireOp",EDGE,"efedae53-bb98-4f59-96c4-10e90d9c938b"),sQuery(id+"F0.wireOp",EDGE,"ba8b6f3e-864d-4f68-a7dd-abca2b296de0"),sQuery(id+"F0.wireOp",EDGE,"CVsaIfdG-YInH-x2fQ-98NN-BXrdCocnHfCg"),sQuery(id+"F0.wireOp",EDGE,"00UZXHGD-P9IW-BGjO-shcO-QPdciv9J71iY"),sQuery(id+"F0.wireOp",EDGE,"a7nKF1FW-fnAZ-2znJ-PXXG-xkcUWXIHMq71"),sQuery(id+"F0.wireOp",EDGE,"E11"),sQuery(id+"F0.wireOp",EDGE,"E12")])],"isStart":true})}),makeQuery(id+"F6.opExtrude","SWEPT_FACE",FACE,{"disambiguationData":[OSD([sQuery(id+"F5.wireOp",EDGE,"E33.left")])]})]}),makeQuery(id+"F8.opExtrude","SWEPT_FACE",FACE,{"disambiguationData":[OSD([sQuery(id+"F7.wireOp",EDGE,"E38")])]})]});
            var Q10;
            Q10=makeQuery(id+"F8.boolean.opBoolean","COPY",EDGE,{"derivedFrom":makeQuery(id+"F8.opExtrude","CAP_EDGE",EDGE,{"disambiguationData":[OSD([sQuery(id+"F7.wireOp",EDGE,"E41")])],"isStart":true})});
            var Q11;
            Q11=makeQuery(id+"F8.boolean.opBoolean","INTERSECT",EDGE,{"derivedFrom":[makeQuery(id+"F6.boolean.opBoolean","MERGE",FACE,{"derivedFrom":[makeQuery(id+"F2.opChamfer","SPLIT",FACE,{"disambiguationData":[OD(0.0)],"derivedFrom":makeQuery(id+"F1.opExtrude","CAP_FACE",FACE,{"disambiguationData":[OSD([sQuery(id+"F0.wireOp",EDGE,"uIqcDY9T-Jbxf-aRt4-gg0R-6jHuYA81VSVm"),sQuery(id+"F0.wireOp",EDGE,"E1"),sQuery(id+"F0.wireOp",EDGE,"E3.bottom"),sQuery(id+"F0.wireOp",EDGE,"E3.top"),sQuery(id+"F0.wireOp",EDGE,"E3.left"),sQuery(id+"F0.wireOp",EDGE,"E4.left"),sQuery(id+"F0.wireOp",EDGE,"rEmcZTTS-8Wlh-duEK-OSmW-KXRGUTnN0HfS"),sQuery(id+"F0.wireOp",EDGE,"E7"),sQuery(id+"F0.wireOp",EDGE,"E9"),sQuery(id+"F0.wireOp",EDGE,"d98010bc-28d3-49a1-b6f3-b908af7b2b54"),sQuery(id+"F0.wireOp",EDGE,"600a4db5-ffff-4d01-831d-9f2957b33658"),sQuery(id+"F0.wireOp",EDGE,"WOJb4iod-LhNt-r6cw-RdzF-wMDI1TDEllQv.bottom"),sQuery(id+"F0.wireOp",EDGE,"WOJb4iod-LhNt-r6cw-RdzF-wMDI1TDEllQv.top"),sQuery(id+"F0.wireOp",EDGE,"NhF1xUkv-KuKP-hu54-HcND-xiFQGb7Tj3II"),sQuery(id+"F0.wireOp",EDGE,"efedae53-bb98-4f59-96c4-10e90d9c938b"),sQuery(id+"F0.wireOp",EDGE,"ba8b6f3e-864d-4f68-a7dd-abca2b296de0"),sQuery(id+"F0.wireOp",EDGE,"CVsaIfdG-YInH-x2fQ-98NN-BXrdCocnHfCg"),sQuery(id+"F0.wireOp",EDGE,"00UZXHGD-P9IW-BGjO-shcO-QPdciv9J71iY"),sQuery(id+"F0.wireOp",EDGE,"a7nKF1FW-fnAZ-2znJ-PXXG-xkcUWXIHMq71"),sQuery(id+"F0.wireOp",EDGE,"E11"),sQuery(id+"F0.wireOp",EDGE,"E12")])],"isStart":true})}),makeQuery(id+"F6.opExtrude","SWEPT_FACE",FACE,{"disambiguationData":[OSD([sQuery(id+"F5.wireOp",EDGE,"E33.left")])]})]}),makeQuery(id+"F8.opExtrude","SWEPT_FACE",FACE,{"disambiguationData":[OSD([sQuery(id+"F7.wireOp",EDGE,"E41")])]})]});
            var Q12;
            {var subQ0=sQuery(id+"F5.wireOp",EDGE,"E33.bottom");var subQ3=sQuery(id+"F5.wireOp",EDGE,"E33.right");Q12=makeQuery(id+"F8.boolean.opBoolean","SPLIT",EDGE,{"disambiguationData":[TD([makeQuery(id+"F8.opExtrude","SWEPT_FACE",FACE,{"disambiguationData":[OSD([sQuery(id+"F7.wireOp",EDGE,"E41")])]})])],"derivedFrom":makeQuery(id+"F6.opExtrude","SWEPT_EDGE",EDGE,{"disambiguationData":[OSD([subQ0,subQ3])]})});}
            var Q13;
            {var subQ0=sQuery(id+"F5.wireOp",EDGE,"E33.left");var subQ1=sQuery(id+"F5.wireOp",EDGE,"E33.bottom");Q13=makeQuery(id+"F8.boolean.opBoolean","SPLIT",EDGE,{"disambiguationData":[TD([makeQuery(id+"F8.opExtrude","SWEPT_FACE",FACE,{"disambiguationData":[OSD([sQuery(id+"F7.wireOp",EDGE,"E41")])]})])],"derivedFrom":makeQuery(id+"F6.opExtrude","SWEPT_EDGE",EDGE,{"disambiguationData":[OSD([subQ1,subQ0])]})});}
            chamfer(context, id + "F9", {"entities" : qUnion([Q0, Q1, Q2, Q3, Q4, Q5, Q6, Q7, Q8, Q9, Q10, Q11, Q12, Q13]), "width" : 1 * mm, "tangentPropagation" : true});
        }
        {
            var Q0;
            Q0=makeQuery(id+"F6.boolean.opBoolean","MERGE",FACE,{"derivedFrom":[makeQuery(id+"F1.opExtrude","CAP_FACE",FACE,{"disambiguationData":[OSD([sQuery(id+"F0.wireOp",EDGE,"E1"),sQuery(id+"F0.wireOp",EDGE,"E3.bottom"),sQuery(id+"F0.wireOp",EDGE,"E3.top"),sQuery(id+"F0.wireOp",EDGE,"E4.left"),sQuery(id+"F0.wireOp",EDGE,"E7"),sQuery(id+"F0.wireOp",EDGE,"E9"),sQuery(id+"F0.wireOp",EDGE,"d98010bc-28d3-49a1-b6f3-b908af7b2b54"),sQuery(id+"F0.wireOp",EDGE,"600a4db5-ffff-4d01-831d-9f2957b33658"),sQuery(id+"F0.wireOp",EDGE,"WOJb4iod-LhNt-r6cw-RdzF-wMDI1TDEllQv.bottom"),sQuery(id+"F0.wireOp",EDGE,"WOJb4iod-LhNt-r6cw-RdzF-wMDI1TDEllQv.top"),sQuery(id+"F0.wireOp",EDGE,"NhF1xUkv-KuKP-hu54-HcND-xiFQGb7Tj3II"),sQuery(id+"F0.wireOp",EDGE,"efedae53-bb98-4f59-96c4-10e90d9c938b"),sQuery(id+"F0.wireOp",EDGE,"ba8b6f3e-864d-4f68-a7dd-abca2b296de0"),sQuery(id+"F0.wireOp",EDGE,"CVsaIfdG-YInH-x2fQ-98NN-BXrdCocnHfCg"),sQuery(id+"F0.wireOp",EDGE,"00UZXHGD-P9IW-BGjO-shcO-QPdciv9J71iY"),sQuery(id+"F0.wireOp",EDGE,"a7nKF1FW-fnAZ-2znJ-PXXG-xkcUWXIHMq71"),sQuery(id+"F0.wireOp",EDGE,"E11"),sQuery(id+"F0.wireOp",EDGE,"E12"),sQuery(id+"F0.wireOp",EDGE,"LoVlnwY0-goBL-XspJ-MOSW-gv1B7iTJkpeO"),sQuery(id+"F0.wireOp",EDGE,"8YUn9cvo-RZEs-pOM1-VRL8-89LIzTiUGwx0"),sQuery(id+"F0.wireOp",EDGE,"y7CVjtlQ-WfPy-SyB8-Xcmz-rx7hH1kh58c1"),sQuery(id+"F0.wireOp",EDGE,"dxAtwFGu-dCJm-7jaL-4A4g-HOkAJ22Vz9y7"),sQuery(id+"F0.wireOp",EDGE,"L5jN4jJu-Q4wT-aSny-XyIM-LaIA1ToUzlHX"),sQuery(id+"F0.wireOp",EDGE,"vGk40aG9-Jj23-V27B-M3qH-pyRGLcxjfKyg"),sQuery(id+"F0.wireOp",EDGE,"G4KyRCB9-ZUby-WLRX-OMVy-VopdA1jCFt6i"),sQuery(id+"F0.wireOp",EDGE,"E23"),sQuery(id+"F0.wireOp",EDGE,"E24"),sQuery(id+"F0.wireOp",EDGE,"KOMAG6Ks-Uhse-fsg6-eFhg-ctIUwGdaKxqe"),sQuery(id+"F0.wireOp",EDGE,"E25"),sQuery(id+"F0.wireOp",EDGE,"E26")])],"isStart":false}),makeQuery(id+"F6.opExtrude","SWEPT_FACE",FACE,{"disambiguationData":[OSD([sQuery(id+"F5.wireOp",EDGE,"E33.right")])]})]});
            var sketch = newSketch(context, id + "F10", { "sketchPlane" : qUnion([Q0])});
            skLineSegment(sketch, "E45", {"start": v(212.8, 227) * mm, "end": v(358.68, -48.13) * mm});
            skLineSegment(sketch, "E46", {"start": v(358.68, -48.13) * mm, "end": v(436.15, -85.54) * mm});
            skLineSegment(sketch, "E47", {"start": v(436.15, -85.54) * mm, "end": v(570.82, 193.32) * mm});
            skLineSegment(sketch, "E48", {"start": v(570.82, 193.32) * mm, "end": v(469.4, 193.32) * mm});
            skLineSegment(sketch, "E49", {"start": v(469.4, 193.32) * mm, "end": v(507.2, 240.98) * mm});
            skLineSegment(sketch, "E50", {"start": v(507.2, 240.98) * mm, "end": v(452.03, 232.66) * mm});
            skLineSegment(sketch, "E51", {"start": v(452.03, 232.66) * mm, "end": v(471.68, 315.8) * mm});
            skLineSegment(sketch, "E52", {"start": v(471.68, 315.8) * mm, "end": v(398.36, 336.21) * mm});
            skLineSegment(sketch, "E53", {"start": v(398.36, 336.21) * mm, "end": v(391.56, 300.69) * mm});
            skLineSegment(sketch, "E54", {"start": v(391.56, 300.69) * mm, "end": v(328.07, 348.3) * mm});
            skLineSegment(sketch, "E55", {"start": v(328.07, 348.3) * mm, "end": v(334.87, 299.17) * mm});
            skLineSegment(sketch, "E56", {"start": v(334.87, 299.17) * mm, "end": v(241.15, 336.97) * mm});
            skLineSegment(sketch, "E57", {"start": v(241.15, 336.97) * mm, "end": v(275.16, 290.1) * mm});
            skLineSegment(sketch, "E58", {"start": v(275.16, 290.1) * mm, "end": v(111.9, 309) * mm});
            skLineSegment(sketch, "E59", {"start": v(111.9, 309) * mm, "end": v(230.57, 247.02) * mm});
            skLineSegment(sketch, "E60", {"start": v(230.57, 247.02) * mm, "end": v(212.8, 227) * mm});
            skSolve(sketch);
        }
        {
            var Q0;
            Q0 = qSketchRegion(id + "F10", true);
            extrude(context, id + "F11", {"entities" : qUnion([Q0]), "operationType" : NewBodyOperationType.REMOVE, "oppositeDirection" : true, "depth" : 500 * mm, "offsetDistance" : 25 * mm});
        }
        {
            var Q0;
            Q0=makeQuery(id+"F6.boolean.opBoolean","MERGE",FACE,{"derivedFrom":[makeQuery(id+"F1.opExtrude","CAP_FACE",FACE,{"disambiguationData":[OSD([sQuery(id+"F0.wireOp",EDGE,"E1"),sQuery(id+"F0.wireOp",EDGE,"E3.bottom"),sQuery(id+"F0.wireOp",EDGE,"E3.top"),sQuery(id+"F0.wireOp",EDGE,"E4.left"),sQuery(id+"F0.wireOp",EDGE,"E7"),sQuery(id+"F0.wireOp",EDGE,"E9"),sQuery(id+"F0.wireOp",EDGE,"d98010bc-28d3-49a1-b6f3-b908af7b2b54"),sQuery(id+"F0.wireOp",EDGE,"600a4db5-ffff-4d01-831d-9f2957b33658"),sQuery(id+"F0.wireOp",EDGE,"WOJb4iod-LhNt-r6cw-RdzF-wMDI1TDEllQv.bottom"),sQuery(id+"F0.wireOp",EDGE,"WOJb4iod-LhNt-r6cw-RdzF-wMDI1TDEllQv.top"),sQuery(id+"F0.wireOp",EDGE,"NhF1xUkv-KuKP-hu54-HcND-xiFQGb7Tj3II"),sQuery(id+"F0.wireOp",EDGE,"efedae53-bb98-4f59-96c4-10e90d9c938b"),sQuery(id+"F0.wireOp",EDGE,"ba8b6f3e-864d-4f68-a7dd-abca2b296de0"),sQuery(id+"F0.wireOp",EDGE,"CVsaIfdG-YInH-x2fQ-98NN-BXrdCocnHfCg"),sQuery(id+"F0.wireOp",EDGE,"00UZXHGD-P9IW-BGjO-shcO-QPdciv9J71iY"),sQuery(id+"F0.wireOp",EDGE,"a7nKF1FW-fnAZ-2znJ-PXXG-xkcUWXIHMq71"),sQuery(id+"F0.wireOp",EDGE,"E11"),sQuery(id+"F0.wireOp",EDGE,"E12"),sQuery(id+"F0.wireOp",EDGE,"LoVlnwY0-goBL-XspJ-MOSW-gv1B7iTJkpeO"),sQuery(id+"F0.wireOp",EDGE,"8YUn9cvo-RZEs-pOM1-VRL8-89LIzTiUGwx0"),sQuery(id+"F0.wireOp",EDGE,"y7CVjtlQ-WfPy-SyB8-Xcmz-rx7hH1kh58c1"),sQuery(id+"F0.wireOp",EDGE,"dxAtwFGu-dCJm-7jaL-4A4g-HOkAJ22Vz9y7"),sQuery(id+"F0.wireOp",EDGE,"L5jN4jJu-Q4wT-aSny-XyIM-LaIA1ToUzlHX"),sQuery(id+"F0.wireOp",EDGE,"vGk40aG9-Jj23-V27B-M3qH-pyRGLcxjfKyg"),sQuery(id+"F0.wireOp",EDGE,"G4KyRCB9-ZUby-WLRX-OMVy-VopdA1jCFt6i"),sQuery(id+"F0.wireOp",EDGE,"E23"),sQuery(id+"F0.wireOp",EDGE,"E24"),sQuery(id+"F0.wireOp",EDGE,"KOMAG6Ks-Uhse-fsg6-eFhg-ctIUwGdaKxqe"),sQuery(id+"F0.wireOp",EDGE,"E25"),sQuery(id+"F0.wireOp",EDGE,"E26")])],"isStart":false}),makeQuery(id+"F6.opExtrude","SWEPT_FACE",FACE,{"disambiguationData":[OSD([sQuery(id+"F5.wireOp",EDGE,"E33.right")])]})]});
            var sketch = newSketch(context, id + "F12", { "sketchPlane" : qUnion([Q0])});
            skLineSegment(sketch, "E61", {"start": v(283.7, -14) * mm, "end": v(283.7, -1) * mm});
            skLineSegment(sketch, "E62", {"start": v(283.7, -1) * mm, "end": v(333.7, -1) * mm});
            skLineSegment(sketch, "E63", {"start": v(333.7, -1) * mm, "end": v(340.59, -14) * mm});
            skLineSegment(sketch, "E64", {"start": v(340.59, -14) * mm, "end": v(283.7, -14) * mm});
            skSolve(sketch);
        }
        {
            var Q0;
            Q0=makeQuery(id+"F6.boolean.opBoolean","MERGE",FACE,{"derivedFrom":[makeQuery(id+"F1.opExtrude","CAP_FACE",FACE,{"disambiguationData":[OSD([sQuery(id+"F0.wireOp",EDGE,"E1"),sQuery(id+"F0.wireOp",EDGE,"E3.bottom"),sQuery(id+"F0.wireOp",EDGE,"E3.top"),sQuery(id+"F0.wireOp",EDGE,"E4.left"),sQuery(id+"F0.wireOp",EDGE,"E7"),sQuery(id+"F0.wireOp",EDGE,"E9"),sQuery(id+"F0.wireOp",EDGE,"E11"),sQuery(id+"F0.wireOp",EDGE,"E12"),sQuery(id+"F0.wireOp",EDGE,"E23"),sQuery(id+"F0.wireOp",EDGE,"E24"),sQuery(id+"F0.wireOp",EDGE,"E25"),sQuery(id+"F0.wireOp",EDGE,"E26"),sQuery(id+"F0.wireOp",EDGE,"E27"),sQuery(id+"F0.wireOp",EDGE,"E28"),sQuery(id+"F0.wireOp",EDGE,"E29"),sQuery(id+"F0.wireOp",EDGE,"E30"),sQuery(id+"F0.wireOp",EDGE,"E31"),sQuery(id+"F0.wireOp",EDGE,"E32")])],"isStart":false}),makeQuery(id+"F6.opExtrude","SWEPT_FACE",FACE,{"disambiguationData":[OSD([sQuery(id+"F5.wireOp",EDGE,"E33.right")])]})]});
            var sketch = newSketch(context, id + "F13", { "sketchPlane" : qUnion([Q0])});
            skLineSegment(sketch, "E65", {"start": v(195.97, 166.26) * mm, "end": v(183.03, 181.51) * mm});
            skLineSegment(sketch, "E66", {"start": v(183.03, 181.51) * mm, "end": v(216.98, 210.32) * mm});
            skLineSegment(sketch, "E67", {"start": v(216.98, 210.32) * mm, "end": v(229.43, 195.64) * mm});
            skLineSegment(sketch, "E68", {"start": v(229.43, 195.64) * mm, "end": v(229.8, 194.96) * mm});
            skLineSegment(sketch, "E69", {"start": v(229.8, 194.96) * mm, "end": v(195.97, 166.26) * mm});
            skSolve(sketch);
        }
        {
            var Q0;
            Q0 = qSketchRegion(id + "F13", true);
            extrude(context, id + "F14", {"entities" : qUnion([Q0]), "operationType" : NewBodyOperationType.ADD, "depth" : 10 * mm, "offsetDistance" : 25 * mm});
        }
        {
            var Q0;
            Q0=makeQuery(id+"F6.boolean.opBoolean","MERGE",FACE,{"derivedFrom":[makeQuery(id+"F1.opExtrude","CAP_FACE",FACE,{"disambiguationData":[OSD([sQuery(id+"F0.wireOp",EDGE,"E1"),sQuery(id+"F0.wireOp",EDGE,"E3.bottom"),sQuery(id+"F0.wireOp",EDGE,"E3.top"),sQuery(id+"F0.wireOp",EDGE,"E4.left"),sQuery(id+"F0.wireOp",EDGE,"E7"),sQuery(id+"F0.wireOp",EDGE,"E9"),sQuery(id+"F0.wireOp",EDGE,"E11"),sQuery(id+"F0.wireOp",EDGE,"E12"),sQuery(id+"F0.wireOp",EDGE,"E23"),sQuery(id+"F0.wireOp",EDGE,"E24"),sQuery(id+"F0.wireOp",EDGE,"E25"),sQuery(id+"F0.wireOp",EDGE,"E26"),sQuery(id+"F0.wireOp",EDGE,"E27"),sQuery(id+"F0.wireOp",EDGE,"E28"),sQuery(id+"F0.wireOp",EDGE,"E29"),sQuery(id+"F0.wireOp",EDGE,"E30"),sQuery(id+"F0.wireOp",EDGE,"E31"),sQuery(id+"F0.wireOp",EDGE,"E32")])],"isStart":true}),makeQuery(id+"F6.opExtrude","SWEPT_FACE",FACE,{"disambiguationData":[OSD([sQuery(id+"F5.wireOp",EDGE,"E33.left")])]})]});
            var sketch = newSketch(context, id + "F15", { "sketchPlane" : qUnion([Q0])});
            skLineSegment(sketch, "E70", {"start": v(-195.97, 166.26) * mm, "end": v(-183.03, 181.51) * mm});
            skLineSegment(sketch, "E71", {"start": v(-183.03, 181.51) * mm, "end": v(-216.98, 210.32) * mm});
            skLineSegment(sketch, "E72", {"start": v(-216.98, 210.32) * mm, "end": v(-229.43, 195.64) * mm});
            skLineSegment(sketch, "E73", {"start": v(-229.43, 195.64) * mm, "end": v(-229.8, 194.96) * mm});
            skLineSegment(sketch, "E74", {"start": v(-229.8, 194.96) * mm, "end": v(-195.97, 166.26) * mm});
            skSolve(sketch);
        }
        {
            var Q0;
            Q0 = qSketchRegion(id + "F15", true);
            extrude(context, id + "F16", {"entities" : qUnion([Q0]), "operationType" : NewBodyOperationType.ADD, "depth" : 10 * mm, "offsetDistance" : 25 * mm});
        }
        {
            var Q0;
            Q0=makeQuery(id+"F16.opExtrude","CAP_FACE",FACE,{"disambiguationData":[OSD([sQuery(id+"F15.wireOp",EDGE,"E70"),sQuery(id+"F15.wireOp",EDGE,"E71"),sQuery(id+"F15.wireOp",EDGE,"E72"),sQuery(id+"F15.wireOp",EDGE,"E73"),sQuery(id+"F15.wireOp",EDGE,"E74")])],"isStart":false});
            var sketch = newSketch(context, id + "F17", { "sketchPlane" : qUnion([Q0])});
            skCircle(sketch, "E75", {"center": v(-214.3, 194.93) * mm, "radius": 5 * mm});
            skSolve(sketch);
        }
        {
            var Q0;
            Q0 = qSketchRegion(id + "F17", true);
            extrude(context, id + "F18", {"entities" : qUnion([Q0]), "operationType" : NewBodyOperationType.ADD, "depth" : 15 * mm, "offsetDistance" : 25 * mm});
        }
        {
            var Q0;
            Q0 = qSketchRegion(id + "F12", true);
            extrude(context, id + "F19", {"entities" : qUnion([Q0]), "operationType" : NewBodyOperationType.ADD, "depth" : 10 * mm, "offsetDistance" : 25 * mm});
        }
        {
            var Q0;
            Q0=makeQuery(id+"F6.boolean.opBoolean","MERGE",FACE,{"derivedFrom":[makeQuery(id+"F1.opExtrude","CAP_FACE",FACE,{"disambiguationData":[OSD([sQuery(id+"F0.wireOp",EDGE,"E1"),sQuery(id+"F0.wireOp",EDGE,"E3.bottom"),sQuery(id+"F0.wireOp",EDGE,"E3.top"),sQuery(id+"F0.wireOp",EDGE,"E4.left"),sQuery(id+"F0.wireOp",EDGE,"E7"),sQuery(id+"F0.wireOp",EDGE,"E9"),sQuery(id+"F0.wireOp",EDGE,"E11"),sQuery(id+"F0.wireOp",EDGE,"E12"),sQuery(id+"F0.wireOp",EDGE,"E23"),sQuery(id+"F0.wireOp",EDGE,"E24"),sQuery(id+"F0.wireOp",EDGE,"E25"),sQuery(id+"F0.wireOp",EDGE,"E26"),sQuery(id+"F0.wireOp",EDGE,"E27"),sQuery(id+"F0.wireOp",EDGE,"E28"),sQuery(id+"F0.wireOp",EDGE,"E29"),sQuery(id+"F0.wireOp",EDGE,"E30"),sQuery(id+"F0.wireOp",EDGE,"E31"),sQuery(id+"F0.wireOp",EDGE,"E32")])],"isStart":true}),makeQuery(id+"F6.opExtrude","SWEPT_FACE",FACE,{"disambiguationData":[OSD([sQuery(id+"F5.wireOp",EDGE,"E33.left")])]})]});
            var sketch = newSketch(context, id + "F20", { "sketchPlane" : qUnion([Q0])});
            skLineSegment(sketch, "E76", {"start": v(-283.7, -1) * mm, "end": v(-283.7, -14) * mm});
            skLineSegment(sketch, "E77", {"start": v(-283.7, -1) * mm, "end": v(-333.7, -1) * mm});
            skLineSegment(sketch, "E78", {"start": v(-333.7, -1) * mm, "end": v(-340.59, -14) * mm});
            skLineSegment(sketch, "E79", {"start": v(-340.59, -14) * mm, "end": v(-283.7, -14) * mm});
            skCircle(sketch, "E80", {"center": v(-318.7, -7.31) * mm, "radius": 5 * mm});
            skSolve(sketch);
        }
        {
            var Q0;
            Q0 = qSketchRegion(id + "F20", true);
            extrude(context, id + "F21", {"entities" : qUnion([Q0]), "operationType" : NewBodyOperationType.ADD, "depth" : 10 * mm, "offsetDistance" : 25 * mm});
        }
        {
            var Q0;
            Q0=makeQuery(id+"F19.opExtrude","CAP_FACE",FACE,{"disambiguationData":[OSD([sQuery(id+"F12.wireOp",EDGE,"E61"),sQuery(id+"F12.wireOp",EDGE,"E62"),sQuery(id+"F12.wireOp",EDGE,"E63"),sQuery(id+"F12.wireOp",EDGE,"E64")])],"isStart":false});
            var sketch = newSketch(context, id + "F22", { "sketchPlane" : qUnion([Q0])});
            skCircle(sketch, "E81", {"center": v(321.7, -7.5) * mm, "radius": 5 * mm});
            skSolve(sketch);
        }
        {
            var Q0;
            Q0 = qSketchRegion(id + "F22", true);
            extrude(context, id + "F23", {"entities" : qUnion([Q0]), "operationType" : NewBodyOperationType.ADD, "depth" : 15 * mm, "offsetDistance" : 25 * mm});
        }
        {
            var Q0;
            Q0=makeQuery(id+"F19.opExtrude","CAP_FACE",FACE,{"disambiguationData":[OSD([sQuery(id+"F12.wireOp",EDGE,"E61"),sQuery(id+"F12.wireOp",EDGE,"E62"),sQuery(id+"F12.wireOp",EDGE,"E63"),sQuery(id+"F12.wireOp",EDGE,"E64")])],"isStart":false});
            var sketch = newSketch(context, id + "F24", { "sketchPlane" : qUnion([Q0])});
            skLineSegment(sketch, "E82", {"start": v(331.83, -1) * mm, "end": v(331.83, -14) * mm});
            skLineSegment(sketch, "E83", {"start": v(331.83, -14) * mm, "end": v(340.59, -14) * mm});
            skLineSegment(sketch, "E84", {"start": v(340.59, -14) * mm, "end": v(333.7, -1) * mm});
            skLineSegment(sketch, "E85", {"start": v(333.7, -1) * mm, "end": v(331.83, -1) * mm});
            skSolve(sketch);
        }
        {
            var Q0;
            Q0 = qSketchRegion(id + "F24", true);
            extrude(context, id + "F25", {"entities" : qUnion([Q0]), "operationType" : NewBodyOperationType.REMOVE, "oppositeDirection" : true, "depth" : 41.6 * mm, "offsetDistance" : 25 * mm});
        }
        {
            var Q0;
            Q0=makeQuery(id+"F1.opExtrude","SWEPT_FACE",FACE,{"disambiguationData":[OSD([sQuery(id+"F0.wireOp",EDGE,"E30")])]});
            var sketch = newSketch(context, id + "F26", { "sketchPlane" : qUnion([Q0])});
            skLineSegment(sketch, "E86", {"start": v(-14.92, -14.08) * mm, "end": v(-0.08, -14.08) * mm});
            skLineSegment(sketch, "E87", {"start": v(-0.08, -14.08) * mm, "end": v(-1, -15) * mm});
            skLineSegment(sketch, "E88", {"start": v(-1, -15) * mm, "end": v(-14, -15) * mm});
            skLineSegment(sketch, "E89", {"start": v(-14, -15) * mm, "end": v(-14.92, -14.08) * mm});
            skSolve(sketch);
        }
        {
            var Q0;
            Q0 = qSketchRegion(id + "F26", true);
            extrude(context, id + "F27", {"entities" : qUnion([Q0]), "operationType" : NewBodyOperationType.REMOVE, "oppositeDirection" : true, "depth" : 25 * mm, "offsetDistance" : 25 * mm});
        }
        {
            var Q0;
            Q0=makeQuery(id+"F27.boolean.opBoolean","COPY",FACE,{"derivedFrom":makeQuery(id+"F27.opExtrude","SWEPT_FACE",FACE,{"disambiguationData":[OSD([sQuery(id+"F26.wireOp",EDGE,"E86")])]})});
            extrude(context, id + "F28", {"entities" : qUnion([Q0]), "operationType" : NewBodyOperationType.REMOVE, "oppositeDirection" : true, "depth" : 2 * mm, "offsetDistance" : 25 * mm});
        }
        {
            var Q0;
            Q0=makeQuery(id+"F21.boolean.opBoolean","SPLIT",FACE,{"disambiguationData":[TD([makeQuery(id+"F21.opExtrude","SWEPT_FACE",FACE,{"disambiguationData":[OSD([sQuery(id+"F20.wireOp",EDGE,"E80")])]})])],"derivedFrom":makeQuery(id+"F6.boolean.opBoolean","MERGE",FACE,{"derivedFrom":[makeQuery(id+"F1.opExtrude","CAP_FACE",FACE,{"disambiguationData":[OSD([sQuery(id+"F0.wireOp",EDGE,"E1"),sQuery(id+"F0.wireOp",EDGE,"E3.bottom"),sQuery(id+"F0.wireOp",EDGE,"E3.top"),sQuery(id+"F0.wireOp",EDGE,"E4.left"),sQuery(id+"F0.wireOp",EDGE,"E7"),sQuery(id+"F0.wireOp",EDGE,"E9"),sQuery(id+"F0.wireOp",EDGE,"E11"),sQuery(id+"F0.wireOp",EDGE,"E12"),sQuery(id+"F0.wireOp",EDGE,"E23"),sQuery(id+"F0.wireOp",EDGE,"E24"),sQuery(id+"F0.wireOp",EDGE,"E25"),sQuery(id+"F0.wireOp",EDGE,"E26"),sQuery(id+"F0.wireOp",EDGE,"E27"),sQuery(id+"F0.wireOp",EDGE,"E28"),sQuery(id+"F0.wireOp",EDGE,"E29"),sQuery(id+"F0.wireOp",EDGE,"E30"),sQuery(id+"F0.wireOp",EDGE,"E31"),sQuery(id+"F0.wireOp",EDGE,"E32")])],"isStart":true}),makeQuery(id+"F6.opExtrude","SWEPT_FACE",FACE,{"disambiguationData":[OSD([sQuery(id+"F5.wireOp",EDGE,"E33.left")])]})]})});
            extrude(context, id + "F29", {"entities" : qUnion([Q0]), "operationType" : NewBodyOperationType.ADD, "depth" : 10 * mm, "offsetDistance" : 25 * mm});
        }
        {
            var Q0;
            Q0=makeQuery(id+"F29.boolean.opBoolean","MERGE",FACE,{"derivedFrom":[makeQuery(id+"F21.opExtrude","CAP_FACE",FACE,{"disambiguationData":[OSD([sQuery(id+"F20.wireOp",EDGE,"E76"),sQuery(id+"F20.wireOp",EDGE,"E77"),sQuery(id+"F20.wireOp",EDGE,"E78"),sQuery(id+"F20.wireOp",EDGE,"E79"),sQuery(id+"F20.wireOp",EDGE,"E80")])],"isStart":false}),makeQuery(id+"F29.opExtrude","CAP_FACE",FACE,{"disambiguationData":[OSD([sQuery(id+"F0.wireOp",EDGE,"E1"),sQuery(id+"F0.wireOp",EDGE,"E3.bottom"),sQuery(id+"F0.wireOp",EDGE,"E3.top"),sQuery(id+"F0.wireOp",EDGE,"E4.left"),sQuery(id+"F0.wireOp",EDGE,"E7"),sQuery(id+"F0.wireOp",EDGE,"E9"),sQuery(id+"F0.wireOp",EDGE,"E11"),sQuery(id+"F0.wireOp",EDGE,"E12"),sQuery(id+"F0.wireOp",EDGE,"E23"),sQuery(id+"F0.wireOp",EDGE,"E24"),sQuery(id+"F0.wireOp",EDGE,"E25"),sQuery(id+"F0.wireOp",EDGE,"E26"),sQuery(id+"F0.wireOp",EDGE,"E27"),sQuery(id+"F0.wireOp",EDGE,"E28"),sQuery(id+"F0.wireOp",EDGE,"E29"),sQuery(id+"F0.wireOp",EDGE,"E30"),sQuery(id+"F0.wireOp",EDGE,"E31"),sQuery(id+"F0.wireOp",EDGE,"E32"),sQuery(id+"F5.wireOp",EDGE,"E33.left")])],"isStart":false})]});
            var sketch = newSketch(context, id + "F30", { "sketchPlane" : qUnion([Q0])});
            skCircle(sketch, "E90", {"center": v(-321.83, -7.5) * mm, "radius": 5 * mm});
            skSolve(sketch);
        }
        {
            var Q0;
            Q0 = qSketchRegion(id + "F30", true);
            extrude(context, id + "F31", {"entities" : qUnion([Q0]), "operationType" : NewBodyOperationType.ADD, "depth" : 15 * mm, "offsetDistance" : 25 * mm});
        }
        {
            var Q0;
            Q0=makeQuery(id+"F14.opExtrude","CAP_FACE",FACE,{"disambiguationData":[OSD([sQuery(id+"F13.wireOp",EDGE,"E65"),sQuery(id+"F13.wireOp",EDGE,"E66"),sQuery(id+"F13.wireOp",EDGE,"E67"),sQuery(id+"F13.wireOp",EDGE,"E68"),sQuery(id+"F13.wireOp",EDGE,"E69")])],"isStart":false});
            var sketch = newSketch(context, id + "F32", { "sketchPlane" : qUnion([Q0])});
            skCircle(sketch, "E91", {"center": v(214.3, 194.93) * mm, "radius": 5 * mm});
            skSolve(sketch);
        }
        {
            var Q0;
            Q0 = qSketchRegion(id + "F32", true);
            extrude(context, id + "F33", {"entities" : qUnion([Q0]), "operationType" : NewBodyOperationType.ADD, "depth" : 15 * mm, "offsetDistance" : 25 * mm});
        }
    });
